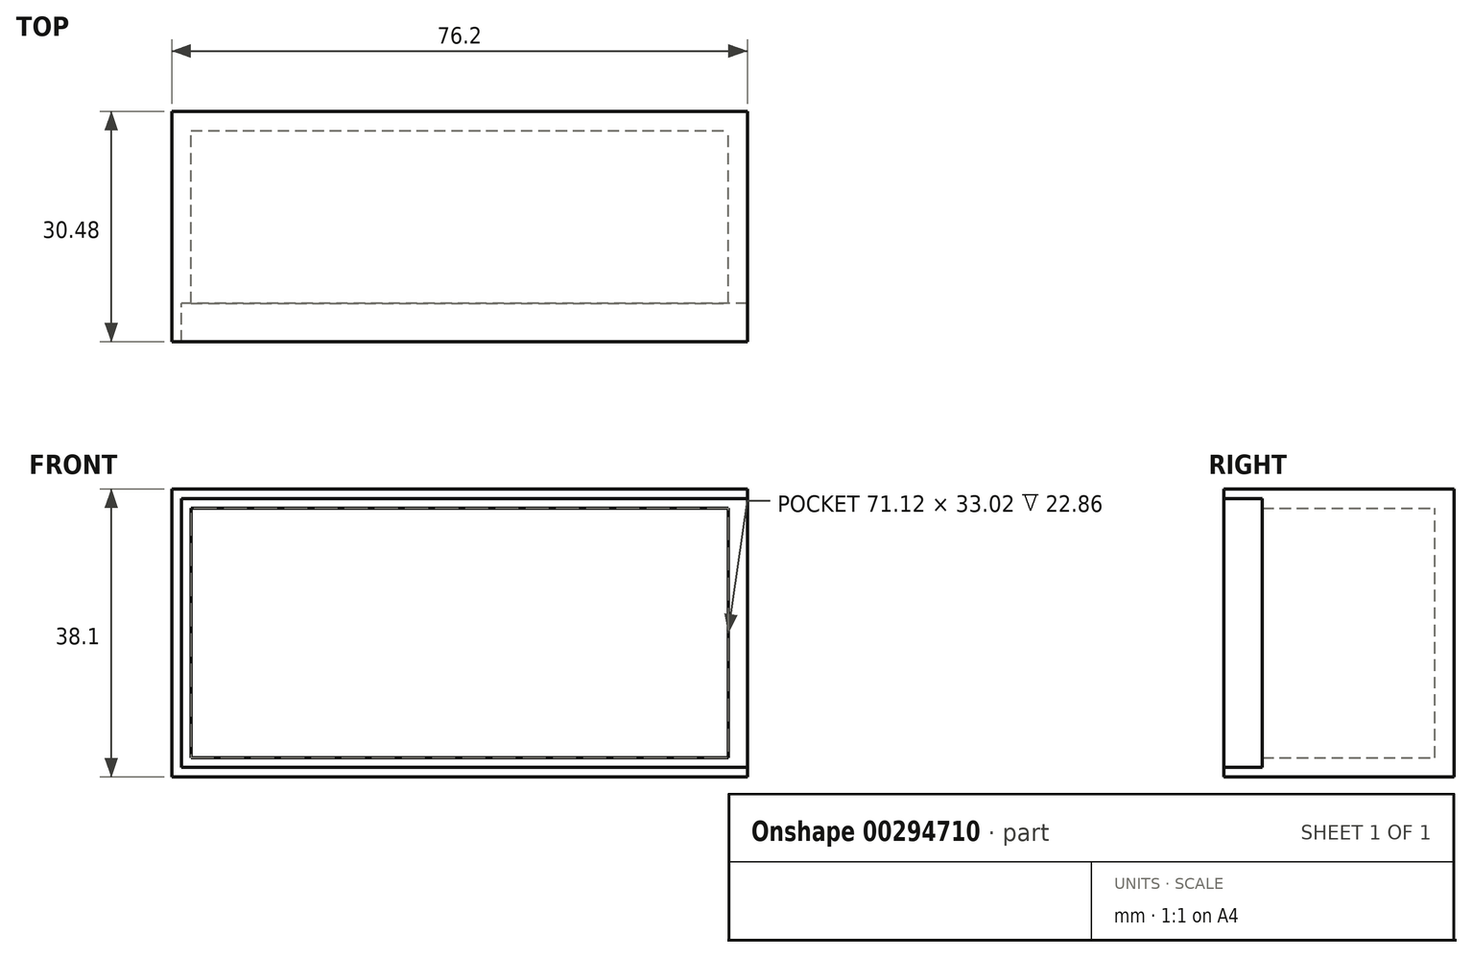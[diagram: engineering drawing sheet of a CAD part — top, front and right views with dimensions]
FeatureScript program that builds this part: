
annotation { "Feature Type Name" : "Feature", "Feature Type Description" : "" }
export const myFeature = defineFeature(function(context is Context, id is Id, definition is map)
    precondition{}
    {
        {
            var Q0;
            Q0=qCreatedBy(makeId("Front.planeOp"),FACE);
            var sketch = newSketch(context, id + "F0", { "sketchPlane" : qUnion([Q0])});
            skLineSegment(sketch, "E0.bottom", {"start": v(0, 0) * mm, "end": v(76.2, 0) * mm});
            skLineSegment(sketch, "E0.top", {"start": v(0, 38.1) * mm, "end": v(76.2, 38.1) * mm});
            skLineSegment(sketch, "E0.left", {"start": v(0, 0) * mm, "end": v(0, 38.1) * mm});
            skLineSegment(sketch, "E0.right", {"start": v(76.2, 0) * mm, "end": v(76.2, 38.1) * mm});
            skSolve(sketch);
        }
        {
            var Q0;
            Q0 = qSketchRegion(id + "F0", true);
            extrude(context, id + "F1", {"entities" : qUnion([Q0]), "depth" : 25.4 * mm});
        }
        {
            var Q0;
            Q0=makeQuery(id+"F1.opExtrude","CAP_FACE",FACE,{"disambiguationData":[OSD([sQuery(id+"F0.wireOp",EDGE,"E0.bottom"),sQuery(id+"F0.wireOp",EDGE,"E0.top"),sQuery(id+"F0.wireOp",EDGE,"E0.left"),sQuery(id+"F0.wireOp",EDGE,"E0.right")])],"isStart":false});
            shell(context, id + "F2", {"entities" : qUnion([Q0]), "thickness" : 2.54 * mm});
        }
        {
            var Q0;
            Q0=makeQuery(id+"F1.opExtrude","CAP_FACE",FACE,{"disambiguationData":[OSD([sQuery(id+"F0.wireOp",EDGE,"E0.bottom"),sQuery(id+"F0.wireOp",EDGE,"E0.top"),sQuery(id+"F0.wireOp",EDGE,"E0.left"),sQuery(id+"F0.wireOp",EDGE,"E0.right")])],"isStart":false});
            var sketch = newSketch(context, id + "F3", { "sketchPlane" : qUnion([Q0])});
            skLineSegment(sketch, "E1", {"start": v(76.2, 36.83) * mm, "end": v(1.27, 36.83) * mm});
            skLineSegment(sketch, "E2", {"start": v(76.2, 1.27) * mm, "end": v(1.27, 1.27) * mm});
            skLineSegment(sketch, "E3", {"start": v(1.27, 36.83) * mm, "end": v(1.27, 1.27) * mm});
            skPoint(sketch, "E4.orphan", {"position": v(0, 1.27) * mm});
            skLineSegment(sketch, "E5", {"start": v(0, 38.1) * mm, "end": v(0, 0) * mm});
            skLineSegment(sketch, "E6", {"start": v(0, 0) * mm, "end": v(76.2, 0) * mm});
            skLineSegment(sketch, "E7", {"start": v(76.2, 0) * mm, "end": v(76.2, 1.27) * mm});
            skLineSegment(sketch, "E8", {"start": v(76.2, 36.83) * mm, "end": v(76.2, 38.1) * mm});
            skLineSegment(sketch, "E9", {"start": v(76.2, 38.1) * mm, "end": v(0, 38.1) * mm});
            skSolve(sketch);
        }
        {
            var Q0;
            Q0 = qSketchRegion(id + "F3", true);
            extrude(context, id + "F4", {"entities" : qUnion([Q0]), "operationType" : NewBodyOperationType.ADD, "depth" : 5.08 * mm});
        }
    });
